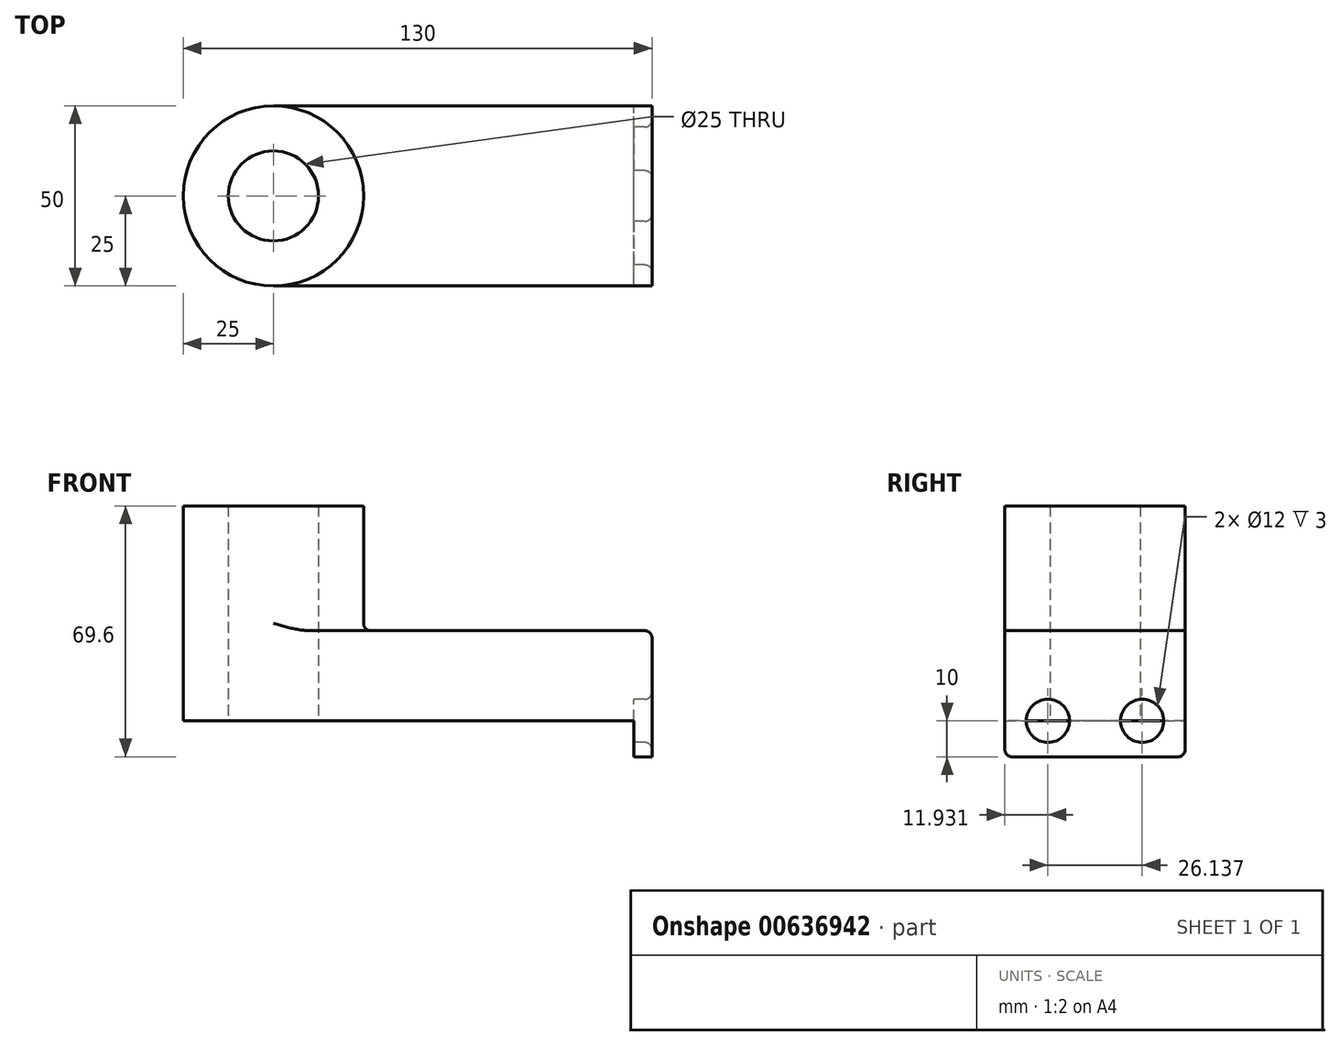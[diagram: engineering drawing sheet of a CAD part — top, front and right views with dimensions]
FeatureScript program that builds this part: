
annotation { "Feature Type Name" : "Feature", "Feature Type Description" : "" }
export const myFeature = defineFeature(function(context is Context, id is Id, definition is map)
    precondition{}
    {
        {
            var Q0;
            Q0=qCreatedBy(makeId("Top.planeOp"),FACE);
            var sketch = newSketch(context, id + "F0", { "sketchPlane" : qUnion([Q0])});
            skLineSegment(sketch, "E0.bottom", {"start": v(50, -25) * mm, "end": v(-50, -25) * mm});
            skLineSegment(sketch, "E0.top", {"start": v(50, 25) * mm, "end": v(-50, 25) * mm});
            skLineSegment(sketch, "E0.left", {"start": v(50, -25) * mm, "end": v(50, 25) * mm});
            skLineSegment(sketch, "E0.right", {"start": v(-50, -25) * mm, "end": v(-50, 25) * mm});
            skPoint(sketch, "E0.middle", {"position": v(0, 0) * mm});
            skCircle(sketch, "E1", {"center": v(-50, 0) * mm, "radius": 25 * mm});
            skCircle(sketch, "E2", {"center": v(-50, 0) * mm, "radius": 12.5 * mm});
            skSolve(sketch);
        }
        {
            var Q0;
            Q0 = qSketchRegion(id + "F0", true);
            extrude(context, id + "F1", {"entities" : qUnion([Q0]), "depth" : 25 * mm, "offsetDistance" : 25 * mm});
        }
        {
            var Q0;
            {var subQ1=sQuery(id+"F0.wireOp",EDGE,"E0.right");var subQ3=sQuery(id+"F0.wireOp",EDGE,"E2");var subQ4=makeQuery(id+"F0.imprint","INTERSECT",VERTEX,{"disambiguationData":[OD(0.0)],"derivedFrom":[subQ1,subQ3]});Q0=makeQuery(id+"F0.imprint","IMPRINT",FACE,{"disambiguationData":[TD([[makeQuery(id+"F0.imprint","IMPRINT",EDGE,{"disambiguationData":[TD([[subQ4,1.0]])],"derivedFrom":subQ3}),-1.0]])]});}
            var Q1;
            {var subQ1=sQuery(id+"F0.wireOp",EDGE,"E0.right");var subQ3=sQuery(id+"F0.wireOp",EDGE,"E2");var subQ4=makeQuery(id+"F0.imprint","INTERSECT",VERTEX,{"disambiguationData":[OD(0.0)],"derivedFrom":[subQ1,subQ3]});Q1=makeQuery(id+"F0.imprint","IMPRINT",FACE,{"disambiguationData":[TD([[makeQuery(id+"F0.imprint","IMPRINT",EDGE,{"disambiguationData":[TD([[subQ4,-1.0]])],"derivedFrom":subQ3}),-1.0]])]});}
            extrude(context, id + "F2", {"entities" : qUnion([Q0, Q1]), "operationType" : NewBodyOperationType.ADD, "depth" : 59.6 * mm, "offsetDistance" : 25 * mm});
        }
        {
            var Q0;
            Q0=makeQuery(id+"F1.opExtrude","SWEPT_FACE",FACE,{"disambiguationData":[OSD([sQuery(id+"F0.wireOp",EDGE,"E0.left")])]});
            var sketch = newSketch(context, id + "F3", { "sketchPlane" : qUnion([Q0])});
            skLineSegment(sketch, "E3.bottom", {"start": v(-25, 25) * mm, "end": v(25, 25) * mm});
            skLineSegment(sketch, "E3.top", {"start": v(-25, -10) * mm, "end": v(25, -10) * mm});
            skLineSegment(sketch, "E3.left", {"start": v(-25, 25) * mm, "end": v(-25, -10) * mm});
            skLineSegment(sketch, "E3.right", {"start": v(25, 25) * mm, "end": v(25, -10) * mm});
            skCircle(sketch, "E4", {"center": v(-13.07, 0) * mm, "radius": 6 * mm});
            skLineSegment(sketch, "E5", {"start": v(0, 17.2) * mm, "end": v(0, -10) * mm, "construction": true});
            skPoint(sketch, "E5.startSnap0", {"position": v(0, 25) * mm});
            skCircle(sketch, "E6.MirrorC", {"center": v(13.07, 0) * mm, "radius": 6 * mm});
            skSolve(sketch);
        }
        {
            var Q0;
            Q0 = qSketchRegion(id + "F3", true);
            extrude(context, id + "F4", {"entities" : qUnion([Q0]), "operationType" : NewBodyOperationType.ADD, "depth" : 5 * mm, "offsetDistance" : 25 * mm});
        }
        {
            var Q0;
            {var subQ0=sQuery(id+"F0.wireOp",EDGE,"E1");Q0=makeQuery(id+"F2.boolean.opBoolean","INTERSECT",EDGE,{"derivedFrom":[makeQuery(id+"F1.opExtrude","CAP_FACE",FACE,{"disambiguationData":[OSD([sQuery(id+"F0.wireOp",EDGE,"E0.bottom"),sQuery(id+"F0.wireOp",EDGE,"E0.top"),sQuery(id+"F0.wireOp",EDGE,"E0.left"),subQ0,sQuery(id+"F0.wireOp",EDGE,"E2")])],"isStart":false}),makeQuery(id+"F2.opExtrude","SWEPT_FACE",FACE,{"disambiguationData":[OSD([subQ0])]})]});}
            var Q1;
            Q1=makeQuery(id+"F4.opExtrude","CAP_EDGE",EDGE,{"disambiguationData":[OSD([sQuery(id+"F3.wireOp",EDGE,"E3.bottom")])],"isStart":false});
            var Q2;
            Q2=makeQuery(id+"F4.opExtrude","SWEPT_EDGE",EDGE,{"disambiguationData":[OSD([sQuery(id+"F3.wireOp",EDGE,"E3.top"),sQuery(id+"F3.wireOp",EDGE,"E3.left")])]});
            var Q3;
            Q3=makeQuery(id+"F4.opExtrude","SWEPT_EDGE",EDGE,{"disambiguationData":[OSD([sQuery(id+"F3.wireOp",EDGE,"E3.top"),sQuery(id+"F3.wireOp",EDGE,"E3.right")])]});
            var Q4;
            Q4=makeQuery(id+"F4.opExtrude","CAP_EDGE",EDGE,{"disambiguationData":[OSD([sQuery(id+"F3.wireOp",EDGE,"E4")])],"isStart":false});
            var Q5;
            Q5=makeQuery(id+"F4.opExtrude","CAP_EDGE",EDGE,{"disambiguationData":[OSD([sQuery(id+"F3.wireOp",EDGE,"E6.MirrorC")])],"isStart":false});
            fillet(context, id + "F5", {"entities" : qUnion([Q0, Q1, Q2, Q3, Q4, Q5]), "radius" : 2 * mm, "tangentPropagation" : true, "allowEdgeOverflow" : false});
        }
    });
